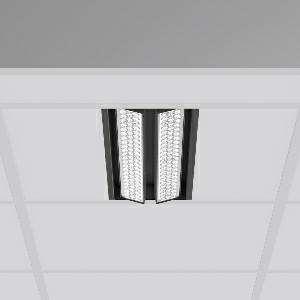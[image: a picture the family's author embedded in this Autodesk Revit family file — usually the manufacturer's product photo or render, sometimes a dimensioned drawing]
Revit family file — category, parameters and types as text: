
# Revit family: tx-move_901733_003_1_76_3c8a
name_source: partatom
category: Lighting Fixtures
units: mm (PartAtom-declared; Revit-internal decimal feet)

## family parameters
Cut with Voids When Loaded = No
Host = Face
Light Source = No
Part Type = Normal
Room Calculation Point = No
Round Connector Dimension = Use Diameter
Shared = No

## types (1)
- MultiLumen 1 (1 x LED Modul 840, 2850 lm, 4000)
    Apparent Load = 35 VA
    Approval mark = CE
    CIE Flux Codes = 77 96 99 100 100
    Color Rendering = 80
    Color Temperature = 4000
    Default Elevation = 1800 mm
    Description = Series: TX-MOVE
Einlege/Einbau-Flächenstrahler. Housing: sheet steel, powder-coated. 2xSwivel range: 90°. High-efficiency LED units with optimum light control thanks to clear plastic (PC) lens optics. Spezielle Mikrostrukturen reduzieren Gelbsaum. Symmetrical light distribution. Suitable for laying in grid ceiling module 600. Connected converter included in separate gearbox.Suitable for through-wiring.MultiLumen: Luminous flux adjustable in 3 steps. Accessories: Mounting frame for installation in suspended ceilings. Environmentally friendly and resource-saving due to replaceable and recyclable components. 
Colour: deep black, matt (RAL 9005)
Length: 597 mm
Width: 190 mm
Height: 39 mm
Cut-out length: 577.5 mm
Cut-out width: 174 mm
Recess height: 100 mm
Lamp: LED
Socket: without socket
Colour temperature: 4000K
Colour rendering index (CRI): 80
System power: 35 W
Rated luminous flux: 5700 lm
Luminous efficiency: 163 lm/W
System power 2: 47 W
Rated luminous flux 2: 7450 lm
Luminous efficiency 2: 159 lm/W
System power 3: 68 W
Rated luminous flux 3: 10200 lm
Luminous efficiency 3: 150 lm/W
Control gear: Dimmable EVG, DALI
Protection class: I
Type of protection: IP 20
    Height = 0 mm  [stored 0 ft]
    Lamp = 1 x LED Modul 840
    Lamp Light Flux = 2850 lm
    Lamp count = 1
    Length = 597 mm
    Lifetime = 50000 h
    Luminous efficacy = 163 lm/W
    Manufacturer = RZB
    ModVariant = No
    Model = 901733.003.1.76
    Mounting Place = Ceiling, Wall
    Mounting Type = Recessed
    Number of Poles = 1
    OnlyDefault = Yes
    Power Factor = 1
    Product Name = TX-MOVE
    Product group = Recessed projectors
    ProductGroupID = 401
    Protection Class = Protection class I
    Protection Degree = IP 20
    RLX_Detail_Level = 1
    RLX_Emergency_Light_Flux = 0 lm
    RLX_Emergency_Type = 0
    RLX_Emergency_Type_DB = No
    RlxData = <blob elided: 36929 chars, md5=82698230>
    Socket = socket
    Standby Power = 0 W
    System Light Flux = 5700 lm
    System Power = 35 W
    Type Comments = MultiLumen 1
    Type Image = 901733.003.jpg
    URL = http://relux.com
    VarID = multilumen_1
    Voltage = 230 V
    Voltage Range = 220-240 V
    Weight = 0.00 kg
    Width = 190 mm  [stored 0.62336 ft]

note: [stored X ft] marks values corroborated as IEEE doubles in the binary element streams (Revit-internal decimal feet)

## geometry (parser evidence)
native form markers: Blend x4, Sweep x16
no freeform markers — native parametric forms only
